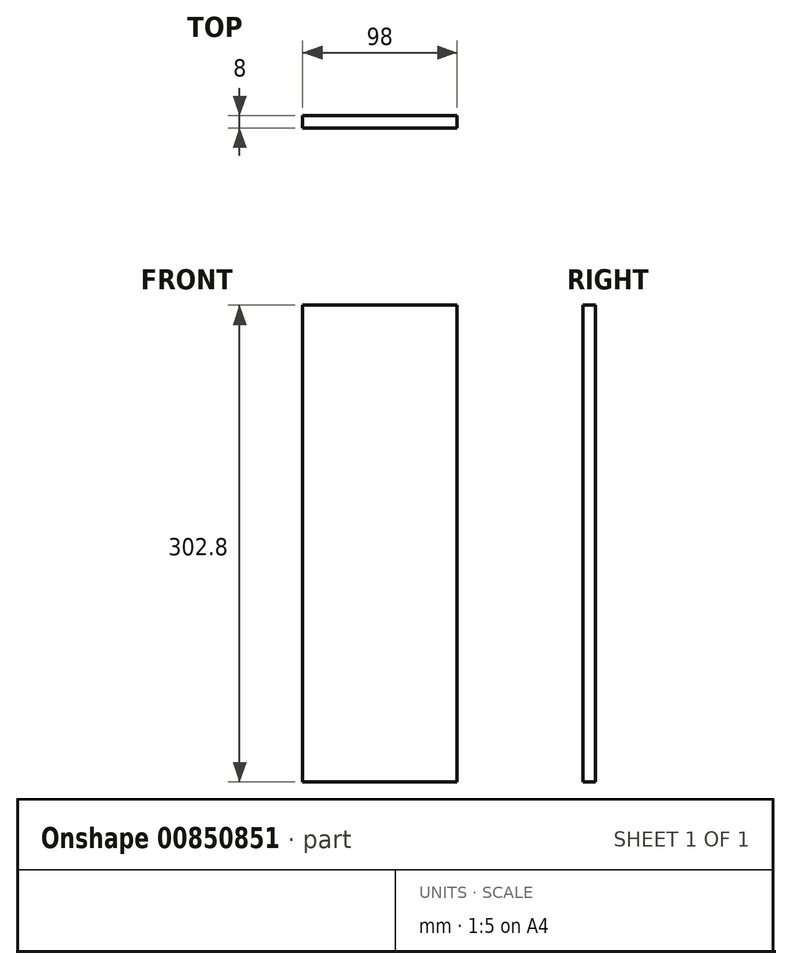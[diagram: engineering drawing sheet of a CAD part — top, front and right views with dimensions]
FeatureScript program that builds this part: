
annotation { "Feature Type Name" : "Feature", "Feature Type Description" : "" }
export const myFeature = defineFeature(function(context is Context, id is Id, definition is map)
    precondition{}
    {
        {
            var Q0;
            Q0=qCreatedBy(makeId("Front.planeOp"),FACE);
            var sketch = newSketch(context, id + "F0", { "sketchPlane" : qUnion([Q0])});
            skLineSegment(sketch, "E0.bottom", {"start": v(-125.57, 200.9) * mm, "end": v(-27.57, 200.9) * mm});
            skLineSegment(sketch, "E0.top", {"start": v(-125.57, -101.9) * mm, "end": v(-27.57, -101.9) * mm});
            skLineSegment(sketch, "E0.left", {"start": v(-125.57, 200.9) * mm, "end": v(-125.57, -101.9) * mm});
            skLineSegment(sketch, "E0.right", {"start": v(-27.57, 200.9) * mm, "end": v(-27.57, -101.9) * mm});
            skSolve(sketch);
        }
        {
            var Q0;
            Q0=makeQuery(id+"F0.imprint","IMPRINT",FACE,{"disambiguationData":[TD([[makeQuery(id+"F0.imprint","IMPRINT",EDGE,{"derivedFrom":sQuery(id+"F0.wireOp",EDGE,"E0.bottom")}),-1.0]])]});
            extrude(context, id + "F1", {"entities" : qUnion([Q0]), "depth" : 8 * mm, "offsetDistance" : 25.4 * mm});
        }
    });
